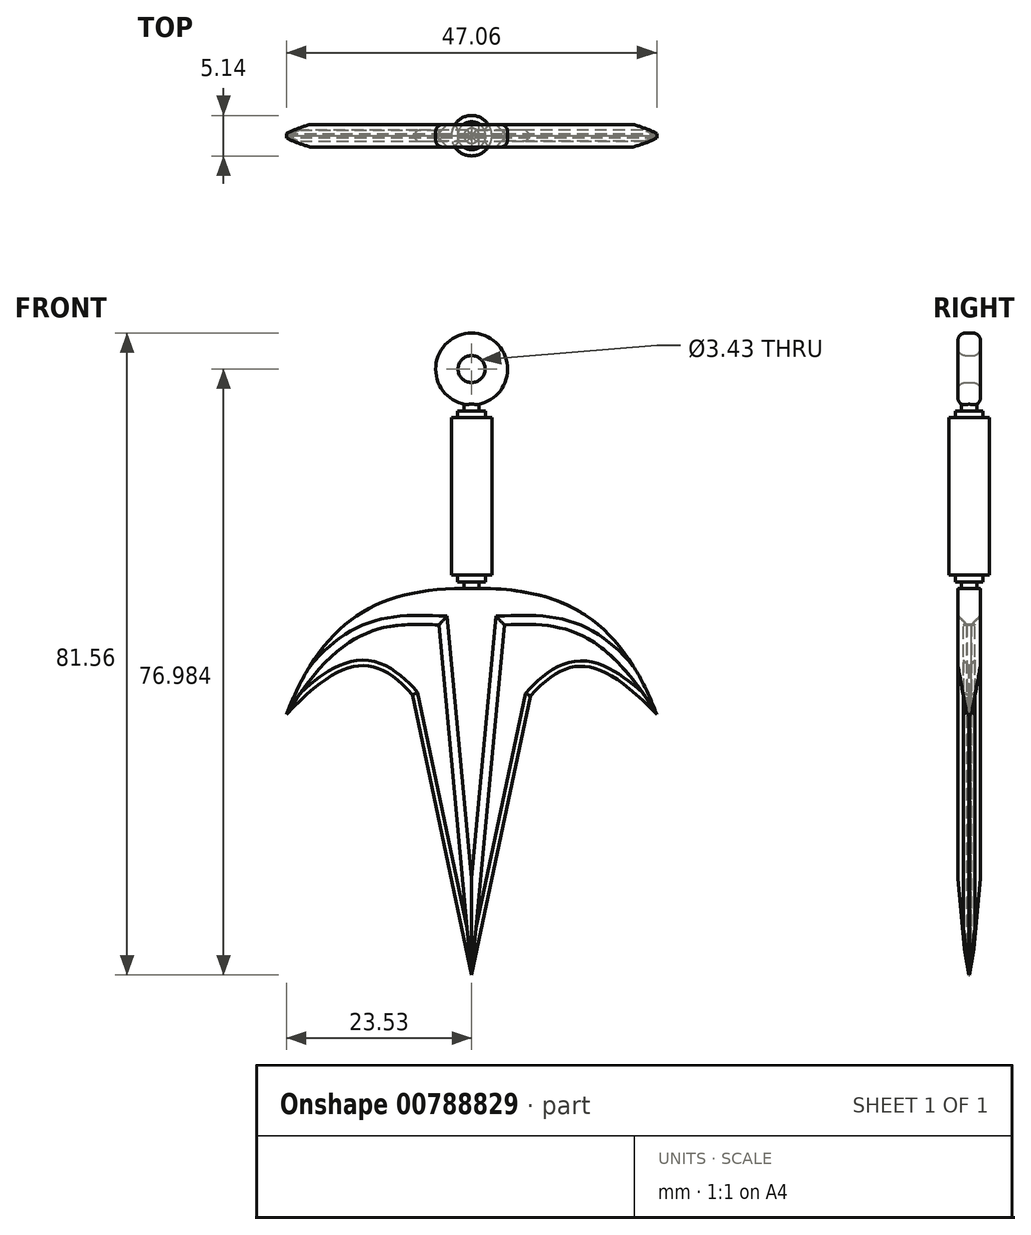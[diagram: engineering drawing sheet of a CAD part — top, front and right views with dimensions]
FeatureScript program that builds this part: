
annotation { "Feature Type Name" : "Feature", "Feature Type Description" : "" }
export const myFeature = defineFeature(function(context is Context, id is Id, definition is map)
    precondition{}
    {
        {
            var Q0;
            Q0=qCreatedBy(makeId("Front.planeOp"),FACE);
            var sketch = newSketch(context, id + "F0", { "sketchPlane" : qUnion([Q0])});
            skLineSegment(sketch, "E0", {"start": v(-2.15, 10.52) * mm, "end": v(2.15, 10.5) * mm});
            skFitSpline(sketch, "E1", {"points": [v(-2.15, 10.52) * mm, v(-52.28, -25.05) * mm], "startDerivative": vector(-77.64, 0.41) * mm, "endDerivative": vector(-28.93, -75.16) * mm});
            skFitSpline(sketch, "E2.MirrorCS", {"points": [v(2.15, 10.52) * mm, v(52.28, -25.05) * mm], "startDerivative": vector(77.64, 0.41) * mm, "endDerivative": vector(28.93, -75.16) * mm});
            skFitSpline(sketch, "E3", {"points": [v(-52.28, -25.05) * mm, v(-16.63, -19.48) * mm], "startDerivative": vector(47.66, 50.06) * mm, "endDerivative": vector(33.37, -37.08) * mm});
            skFitSpline(sketch, "E4.MirrorCS", {"points": [v(52.28, -25.05) * mm, v(16.62, -19.8) * mm], "startDerivative": vector(-47.66, 50.06) * mm, "endDerivative": vector(-33.37, -37.08) * mm});
            skLineSegment(sketch, "E5", {"start": v(-16.63, -19.48) * mm, "end": v(0, -98.6) * mm});
            skLineSegment(sketch, "E6.MirrorCS", {"start": v(16.62, -19.8) * mm, "end": v(0, -98.6) * mm});
            skLineSegment(sketch, "E7", {"start": v(-16.63, -19.48) * mm, "end": v(0, 0) * mm});
            skLineSegment(sketch, "E8.MirrorCS", {"start": v(16.62, -19.8) * mm, "end": v(0, 0) * mm});
            skFitSpline(sketch, "E9", {"points": [v(-52.28, -25.05) * mm, v(0, 0) * mm], "startDerivative": vector(56, 91.77) * mm, "endDerivative": vector(61, 0) * mm});
            skFitSpline(sketch, "E10.MirrorCS", {"points": [v(52.28, -25.05) * mm, v(0, 0) * mm], "startDerivative": vector(-56, 91.77) * mm, "endDerivative": vector(-61, 0) * mm});
            skLineSegment(sketch, "E11", {"start": v(0, -98.6) * mm, "end": v(-8.31, -9.74) * mm});
            skLineSegment(sketch, "E12", {"start": v(0, 10.5) * mm, "end": v(0, -98.6) * mm, "construction": true});
            skLineSegment(sketch, "E13.MirrorCS", {"start": v(0, -98.6) * mm, "end": v(8.31, -9.74) * mm});
            skLineSegment(sketch, "E14", {"start": v(-8.31, -9.74) * mm, "end": v(-9.25, 0.25) * mm});
            skLineSegment(sketch, "E15.MirrorCS", {"start": v(8.31, -9.74) * mm, "end": v(9.25, 0.25) * mm});
            skLineSegment(sketch, "E16", {"start": v(0, 10.5) * mm, "end": v(0, 72.47) * mm, "construction": true});
            skLineSegment(sketch, "E17", {"start": v(2.15, 10.5) * mm, "end": v(2.15, 12.4) * mm});
            skLineSegment(sketch, "E18", {"start": v(2.15, 12.4) * mm, "end": v(3.93, 12.4) * mm});
            skLineSegment(sketch, "E19", {"start": v(3.93, 12.4) * mm, "end": v(3.93, 14.3) * mm});
            skLineSegment(sketch, "E20", {"start": v(3.93, 14.3) * mm, "end": v(5.7, 14.3) * mm});
            skLineSegment(sketch, "E21", {"start": v(5.7, 14.3) * mm, "end": v(5.7, 58.75) * mm});
            skLineSegment(sketch, "E22", {"start": v(5.7, 36.52) * mm, "end": v(-12.22, 36.52) * mm, "construction": true});
            skLineSegment(sketch, "E23.MirrorCS", {"start": v(3.93, 58.74) * mm, "end": v(5.7, 58.75) * mm});
            skLineSegment(sketch, "E24.MirrorCS", {"start": v(2.15, 60.64) * mm, "end": v(3.93, 60.65) * mm});
            skLineSegment(sketch, "E25.MirrorCS", {"start": v(3.93, 60.65) * mm, "end": v(3.93, 58.74) * mm});
            skCircle(sketch, "E26", {"center": v(0, 72.47) * mm, "radius": 10.16 * mm});
            skCircle(sketch, "E27", {"center": v(0, 72.47) * mm, "radius": 3.81 * mm});
            skLineSegment(sketch, "E28", {"start": v(2.14, 62.54) * mm, "end": v(2.15, 60.64) * mm});
            skLineSegment(sketch, "E29", {"start": v(0, 62.31) * mm, "end": v(0, 10.5) * mm});
            skSolve(sketch);
        }
        {
            var Q0;
            Q0=makeQuery(id+"F0.imprint","IMPRINT",FACE,{"disambiguationData":[TD([[makeQuery(id+"F0.imprint","IMPRINT",EDGE,{"derivedFrom":sQuery(id+"F0.wireOp",EDGE,"E27")}),-1.0]])]});
            extrude(context, id + "F1", {"entities" : qUnion([Q0]), "endBound" : BoundingType.SYMMETRIC, "depth" : 6.35 * mm});
        }
        {
            var Q0;
            Q0=makeQuery(id+"F1.opExtrude","CAP_EDGE",EDGE,{"disambiguationData":[OSD([sQuery(id+"F0.wireOp",EDGE,"E26")])],"isStart":false});
            var Q1;
            Q1=makeQuery(id+"F1.opExtrude","CAP_EDGE",EDGE,{"disambiguationData":[OSD([sQuery(id+"F0.wireOp",EDGE,"E26")])],"isStart":true});
            var Q2;
            Q2=makeQuery(id+"F1.opExtrude","CAP_EDGE",EDGE,{"disambiguationData":[OSD([sQuery(id+"F0.wireOp",EDGE,"E27")])],"isStart":true});
            var Q3;
            Q3=makeQuery(id+"F1.opExtrude","CAP_EDGE",EDGE,{"disambiguationData":[OSD([sQuery(id+"F0.wireOp",EDGE,"E27")])],"isStart":false});
            fillet(context, id + "F2", {"entities" : qUnion([Q0, Q1, Q2, Q3]), "radius" : 2.03 * mm, "tangentPropagation" : true, "allowEdgeOverflow" : false});
        }
        {
            var Q0;
            {var subQ2=sQuery(id+"F0.wireOp",EDGE,"E18");Q0=makeQuery(id+"F0.imprint","IMPRINT",FACE,{"disambiguationData":[TD([[makeQuery(id+"F0.imprint","IMPRINT",EDGE,{"derivedFrom":subQ2}),1.0]])]});}
            var Q1;
            Q1=sQuery(id+"F0.wireOp",EDGE,"E29");
            revolve(context, id + "F3", {"operationType" : NewBodyOperationType.ADD, "entities" : qUnion([Q0]), "axis" : qUnion([Q1]), "revolveType" : RevolveType.FULL});
        }
        {
            var Q0;
            {var subQ1=sQuery(id+"F0.wireOp",EDGE,"E1");Q0=makeQuery(id+"F0.imprint","IMPRINT",FACE,{"disambiguationData":[TD([[makeQuery(id+"F0.imprint","IMPRINT",EDGE,{"derivedFrom":subQ1}),1.0]])]});}
            var Q1;
            {var subQ3=sQuery(id+"F0.wireOp",EDGE,"E11");Q1=makeQuery(id+"F0.imprint","IMPRINT",FACE,{"disambiguationData":[TD([[makeQuery(id+"F0.imprint","IMPRINT",EDGE,{"derivedFrom":subQ3}),-1.0]])]});}
            var Q2;
            {var subQ3=sQuery(id+"F0.wireOp",EDGE,"E14");Q2=makeQuery(id+"F0.imprint","IMPRINT",FACE,{"disambiguationData":[TD([[makeQuery(id+"F0.imprint","IMPRINT",EDGE,{"derivedFrom":subQ3}),-1.0]])]});}
            var Q3;
            {var subQ5=sQuery(id+"F0.wireOp",EDGE,"E15.MirrorCS");Q3=makeQuery(id+"F0.imprint","IMPRINT",FACE,{"disambiguationData":[TD([[makeQuery(id+"F0.imprint","IMPRINT",EDGE,{"derivedFrom":subQ5}),1.0]])]});}
            extrude(context, id + "F4", {"entities" : qUnion([Q0, Q1, Q2, Q3]), "endBound" : BoundingType.SYMMETRIC, "depth" : 6.35 * mm});
        }
        {
            var Q0;
            {var subQ0=sQuery(id+"F0.wireOp",EDGE,"E3");Q0=makeQuery(id+"F0.imprint","IMPRINT",FACE,{"disambiguationData":[TD([[makeQuery(id+"F0.imprint","IMPRINT",EDGE,{"derivedFrom":subQ0}),1.0]])]});}
            var Q1;
            {var subQ0=sQuery(id+"F0.wireOp",EDGE,"E5");Q1=makeQuery(id+"F0.imprint","IMPRINT",FACE,{"disambiguationData":[TD([[makeQuery(id+"F0.imprint","IMPRINT",EDGE,{"derivedFrom":subQ0}),1.0]])]});}
            var Q2;
            {var subQ0=sQuery(id+"F0.wireOp",EDGE,"E4.MirrorCS");Q2=makeQuery(id+"F0.imprint","IMPRINT",FACE,{"disambiguationData":[TD([[makeQuery(id+"F0.imprint","IMPRINT",EDGE,{"derivedFrom":subQ0}),-1.0]])]});}
            var Q3;
            {var subQ0=sQuery(id+"F0.wireOp",EDGE,"E6.MirrorCS");Q3=makeQuery(id+"F0.imprint","IMPRINT",FACE,{"disambiguationData":[TD([[makeQuery(id+"F0.imprint","IMPRINT",EDGE,{"derivedFrom":subQ0}),-1.0]])]});}
            extrude(context, id + "F5", {"entities" : qUnion([Q0, Q1, Q2, Q3]), "endBound" : BoundingType.SYMMETRIC, "depth" : 3.17 * mm});
        }
        {
            var Q0;
            Q0=makeQuery(id+"F5.opExtrude","CAP_EDGE",EDGE,{"disambiguationData":[OSD([sQuery(id+"F0.wireOp",EDGE,"E5")])],"isStart":false});
            var Q1;
            Q1=makeQuery(id+"F5.opExtrude","CAP_EDGE",EDGE,{"disambiguationData":[OSD([sQuery(id+"F0.wireOp",EDGE,"E3")])],"isStart":false});
            var Q2;
            Q2=makeQuery(id+"F5.opExtrude","CAP_EDGE",EDGE,{"disambiguationData":[OSD([sQuery(id+"F0.wireOp",EDGE,"E5")])],"isStart":true});
            var Q3;
            Q3=makeQuery(id+"F5.opExtrude","CAP_EDGE",EDGE,{"disambiguationData":[OSD([sQuery(id+"F0.wireOp",EDGE,"E3")])],"isStart":true});
            chamfer(context, id + "F6", {"entities" : qUnion([Q0, Q1, Q2, Q3]), "width" : 1.52 * mm, "tangentPropagation" : true});
        }
        {
            var Q0;
            Q0=makeQuery(id+"F5.opExtrude","CAP_EDGE",EDGE,{"disambiguationData":[OSD([sQuery(id+"F0.wireOp",EDGE,"E6.MirrorCS")])],"isStart":false});
            var Q1;
            Q1=makeQuery(id+"F5.opExtrude","CAP_EDGE",EDGE,{"disambiguationData":[OSD([sQuery(id+"F0.wireOp",EDGE,"E4.MirrorCS")])],"isStart":false});
            var Q2;
            Q2=makeQuery(id+"F5.opExtrude","CAP_EDGE",EDGE,{"disambiguationData":[OSD([sQuery(id+"F0.wireOp",EDGE,"E4.MirrorCS")])],"isStart":true});
            var Q3;
            Q3=makeQuery(id+"F5.opExtrude","CAP_EDGE",EDGE,{"disambiguationData":[OSD([sQuery(id+"F0.wireOp",EDGE,"E6.MirrorCS")])],"isStart":true});
            chamfer(context, id + "F7", {"entities" : qUnion([Q0, Q1, Q2, Q3]), "width" : 1.52 * mm, "tangentPropagation" : true});
        }
        {
            var Q0;
            Q0=makeQuery(id+"F4.opExtrude","CAP_EDGE",EDGE,{"disambiguationData":[OSD([sQuery(id+"F0.wireOp",EDGE,"E7")])],"isStart":false});
            var Q1;
            Q1=makeQuery(id+"F4.opExtrude","CAP_EDGE",EDGE,{"disambiguationData":[OSD([sQuery(id+"F0.wireOp",EDGE,"E11")])],"isStart":false});
            var Q2;
            Q2=makeQuery(id+"F4.opExtrude","CAP_EDGE",EDGE,{"disambiguationData":[OSD([sQuery(id+"F0.wireOp",EDGE,"d41bfb26-c881-4ffa-98e3-99cad1ed0fc00.MirrorCS")])],"isStart":false});
            var Q3;
            Q3=makeQuery(id+"F4.opExtrude","CAP_EDGE",EDGE,{"disambiguationData":[OSD([sQuery(id+"F0.wireOp",EDGE,"E8.MirrorCS")])],"isStart":false});
            var Q4;
            Q4=makeQuery(id+"F4.opExtrude","CAP_EDGE",EDGE,{"disambiguationData":[OSD([sQuery(id+"F0.wireOp",EDGE,"E7")])],"isStart":true});
            var Q5;
            Q5=makeQuery(id+"F4.opExtrude","CAP_EDGE",EDGE,{"disambiguationData":[OSD([sQuery(id+"F0.wireOp",EDGE,"E8.MirrorCS")])],"isStart":true});
            var Q6;
            Q6=makeQuery(id+"F4.opExtrude","CAP_EDGE",EDGE,{"disambiguationData":[OSD([sQuery(id+"F0.wireOp",EDGE,"d41bfb26-c881-4ffa-98e3-99cad1ed0fc00.MirrorCS")])],"isStart":true});
            var Q7;
            Q7=makeQuery(id+"F4.opExtrude","CAP_EDGE",EDGE,{"disambiguationData":[OSD([sQuery(id+"F0.wireOp",EDGE,"E11")])],"isStart":true});
            var Q8;
            Q8=makeQuery(id+"F4.opExtrude","CAP_EDGE",EDGE,{"disambiguationData":[OSD([sQuery(id+"F0.wireOp",EDGE,"E13.MirrorCS")])],"isStart":true});
            var Q9;
            Q9=makeQuery(id+"F4.opExtrude","CAP_EDGE",EDGE,{"disambiguationData":[OSD([sQuery(id+"F0.wireOp",EDGE,"E13.MirrorCS")])],"isStart":false});
            chamfer(context, id + "F8", {"entities" : qUnion([Q0, Q1, Q2, Q3, Q4, Q5, Q6, Q7, Q8, Q9]), "width" : 2.54 * mm, "tangentPropagation" : true});
        }
        {
            var Q0;
            Q0=qCreatedBy(makeId("Right.planeOp"),FACE);
            var sketch = newSketch(context, id + "F9", { "sketchPlane" : qUnion([Q0])});
            skLineSegment(sketch, "E30", {"start": v(0, -99.02) * mm, "end": v(-21.64, -99.02) * mm});
            skLineSegment(sketch, "E31", {"start": v(-21.64, -99.02) * mm, "end": v(-7.44, -55.2) * mm});
            skLineSegment(sketch, "E32", {"start": v(0, -99.02) * mm, "end": v(0, -42.48) * mm, "construction": true});
            skLineSegment(sketch, "E33.MirrorCS", {"start": v(21.64, -99.02) * mm, "end": v(7.44, -55.2) * mm});
            skLineSegment(sketch, "E34.MirrorCS", {"start": v(0, -99.02) * mm, "end": v(21.64, -99.02) * mm});
            skLineSegment(sketch, "E35.MirrorCS", {"start": v(0, -99.02) * mm, "end": v(1, -75.67) * mm});
            skPoint(sketch, "E36.endSnap0", {"position": v(-10.82, -99.02) * mm});
            skLineSegment(sketch, "E37", {"start": v(7.44, -55.2) * mm, "end": v(0, -99.02) * mm});
            skLineSegment(sketch, "E38", {"start": v(-7.44, -55.2) * mm, "end": v(0, -99.02) * mm});
            skSolve(sketch);
        }
        {
            var Q0;
            Q0=qSketchRegion(id+"F9",true);
            extrude(context, id + "F10", {"entities" : qUnion([Q0]), "operationType" : NewBodyOperationType.REMOVE, "endBound" : BoundingType.SYMMETRIC, "oppositeDirection" : true, "depth" : 25.4 * mm});
        }
        {
            var Q0;
            Q0=makeQuery(id+"F4.opExtrude","CAP_EDGE",EDGE,{"disambiguationData":[OSD([sQuery(id+"F0.wireOp",EDGE,"E10.MirrorCS")])],"isStart":true});
            var Q1;
            Q1=makeQuery(id+"F4.opExtrude","CAP_EDGE",EDGE,{"disambiguationData":[OSD([sQuery(id+"F0.wireOp",EDGE,"E9")])],"isStart":true});
            var Q2;
            Q2=makeQuery(id+"F4.opExtrude","CAP_EDGE",EDGE,{"disambiguationData":[OSD([sQuery(id+"F0.wireOp",EDGE,"E10.MirrorCS")])],"isStart":false});
            var Q3;
            Q3=makeQuery(id+"F4.opExtrude","CAP_EDGE",EDGE,{"disambiguationData":[OSD([sQuery(id+"F0.wireOp",EDGE,"E9")])],"isStart":false});
            chamfer(context, id + "F11", {"entities" : qUnion([Q0, Q1, Q2, Q3]), "width" : 2.54 * mm, "tangentPropagation" : true});
        }
        {
            var Q0;
            Q0=makeQuery(id+"F1.opExtrude","SWEPT_BODY",BODY,{"disambiguationData":[OSD([sQuery(id+"F0.wireOp",EDGE,"E26"),sQuery(id+"F0.wireOp",EDGE,"E27")])]});
            var Q1;
            Q1=makeQuery(id+"F4.opExtrude","SWEPT_BODY",BODY,{"disambiguationData":[OSD([sQuery(id+"F0.wireOp",EDGE,"E0"),sQuery(id+"F0.wireOp",EDGE,"E1"),sQuery(id+"F0.wireOp",EDGE,"E2.MirrorCS"),sQuery(id+"F0.wireOp",EDGE,"E9"),sQuery(id+"F0.wireOp",EDGE,"E10.MirrorCS"),sQuery(id+"F0.wireOp",EDGE,"E11"),sQuery(id+"F0.wireOp",EDGE,"E13.MirrorCS"),sQuery(id+"F0.wireOp",EDGE,"E14"),sQuery(id+"F0.wireOp",EDGE,"E15.MirrorCS"),sQuery(id+"F0.wireOp",EDGE,"E17")])]});
            var Q2;
            Q2=makeQuery(id+"F5.opExtrude","SWEPT_BODY",BODY,{"disambiguationData":[OSD([sQuery(id+"F0.wireOp",EDGE,"E3"),sQuery(id+"F0.wireOp",EDGE,"E5"),sQuery(id+"F0.wireOp",EDGE,"E9"),sQuery(id+"F0.wireOp",EDGE,"E11"),sQuery(id+"F0.wireOp",EDGE,"E14")])]});
            var Q3;
            Q3=makeQuery(id+"F5.opExtrude","SWEPT_BODY",BODY,{"disambiguationData":[OSD([sQuery(id+"F0.wireOp",EDGE,"E4.MirrorCS"),sQuery(id+"F0.wireOp",EDGE,"E6.MirrorCS"),sQuery(id+"F0.wireOp",EDGE,"E10.MirrorCS"),sQuery(id+"F0.wireOp",EDGE,"E13.MirrorCS"),sQuery(id+"F0.wireOp",EDGE,"E15.MirrorCS")])]});
            var Q4;
            Q4=qCreatedBy(makeId("Origin.pointOp"),VERTEX);
            transform(context, id + "F12", {"entities" : qUnion([Q0, Q1, Q2, Q3]), "transformType" : TransformType.SCALE_UNIFORMLY, "scale" : .45, "scalePoint" : qUnion([Q4]), "makeCopy" : false});
        }
    });
